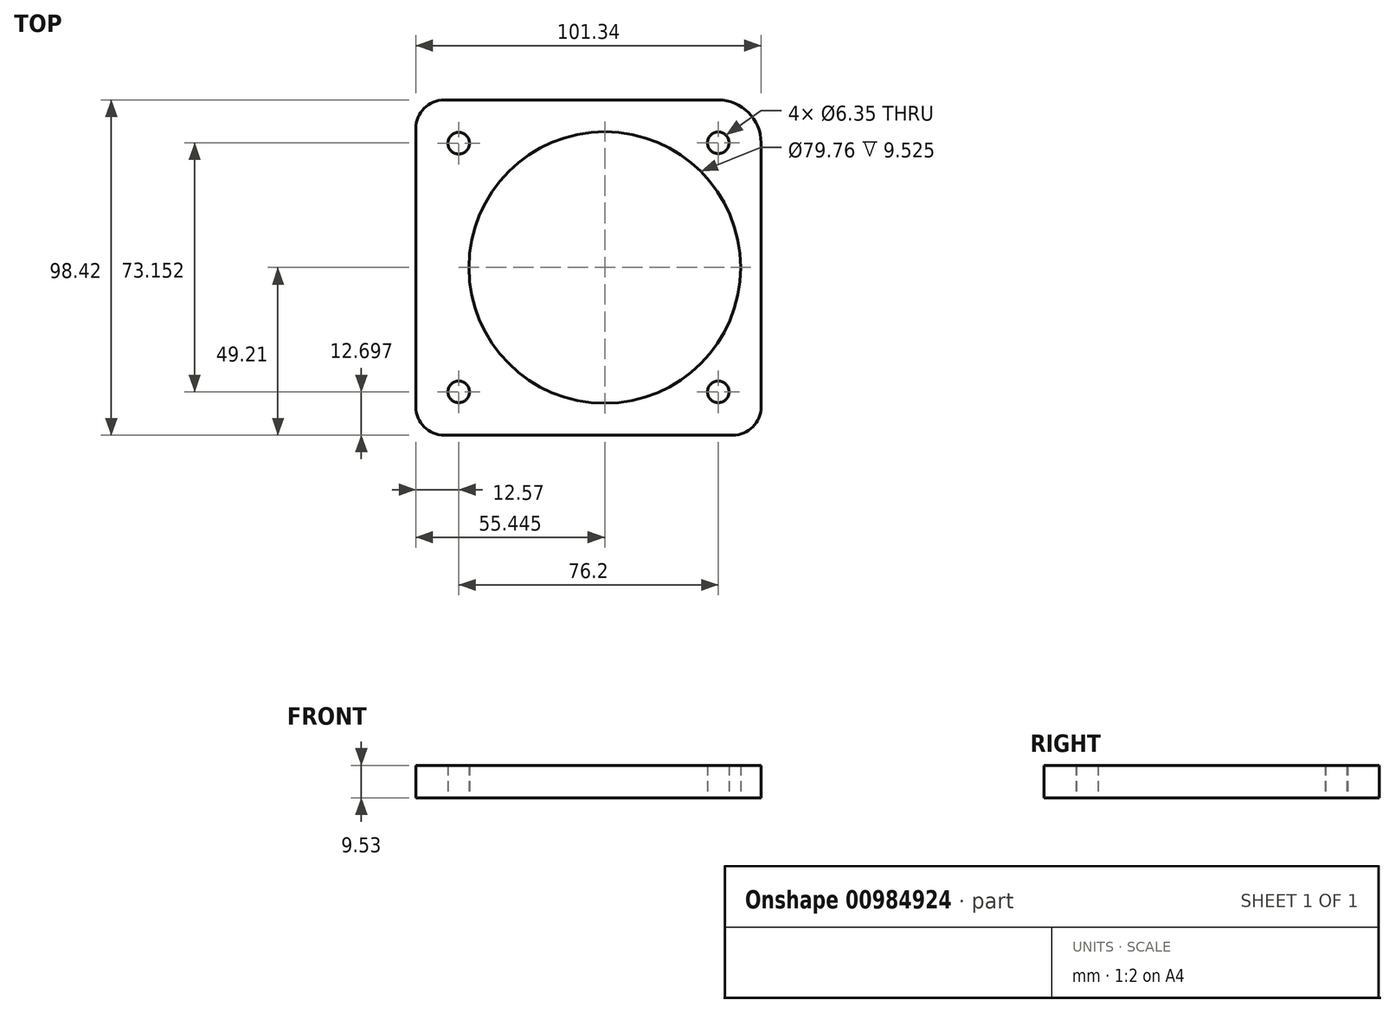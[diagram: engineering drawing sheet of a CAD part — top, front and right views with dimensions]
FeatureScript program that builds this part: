
annotation { "Feature Type Name" : "Feature", "Feature Type Description" : "" }
export const myFeature = defineFeature(function(context is Context, id is Id, definition is map)
    precondition{}
    {
        {
            var Q0;
            Q0=qCreatedBy(makeId("Top.planeOp"),FACE);
            var sketch = newSketch(context, id + "F0", { "sketchPlane" : qUnion([Q0])});
            skLineSegment(sketch, "E0.bottom", {"start": v(-42.39, 49.21) * mm, "end": v(38.1, 49.21) * mm});
            skLineSegment(sketch, "E0.top", {"start": v(-42.39, -49.21) * mm, "end": v(42.39, -49.21) * mm});
            skLineSegment(sketch, "E0.left", {"start": v(-50.67, 40.93) * mm, "end": v(-50.67, -40.93) * mm});
            skLineSegment(sketch, "E0.right", {"start": v(50.67, 36.64) * mm, "end": v(50.67, -40.93) * mm});
            skPoint(sketch, "E0.middle", {"position": v(0, 0) * mm});
            skCircle(sketch, "E1", {"center": v(4.78, 0) * mm, "radius": 39.88 * mm});
            skPoint(sketch, "E2.visualSharp", {"position": v(-50.67, 49.21) * mm});
            skArc(sketch, "E2.filletArc", {"start": v(-42.39, 49.21) * mm, "mid": v(-48.25, 46.79) * mm, "end": v(-50.67, 40.93) * mm});
            skPoint(sketch, "E3.visualSharp", {"position": v(-50.67, -49.21) * mm});
            skArc(sketch, "E3.filletArc", {"start": v(-50.67, -40.93) * mm, "mid": v(-48.25, -46.79) * mm, "end": v(-42.39, -49.21) * mm});
            skPoint(sketch, "E4.visualSharp", {"position": v(50.67, -49.21) * mm});
            skArc(sketch, "E4.filletArc", {"start": v(42.39, -49.21) * mm, "mid": v(48.25, -46.79) * mm, "end": v(50.67, -40.93) * mm});
            skPoint(sketch, "E5.visualSharp", {"position": v(50.67, 49.21) * mm});
            skArc(sketch, "E5.filletArc", {"start": v(50.67, 36.64) * mm, "mid": v(47, 45.53) * mm, "end": v(38.1, 49.21) * mm});
            skCircle(sketch, "E6", {"center": v(-38.1, 36.51) * mm, "radius": 3.18 * mm});
            skCircle(sketch, "E7", {"center": v(-38.1, -36.51) * mm, "radius": 3.18 * mm});
            skCircle(sketch, "E8", {"center": v(38.1, -36.51) * mm, "radius": 3.18 * mm});
            skCircle(sketch, "E9", {"center": v(38.1, 36.64) * mm, "radius": 3.18 * mm});
            skSolve(sketch);
        }
        {
            var Q0;
            Q0=makeQuery(id+"F0.imprint","IMPRINT",FACE,{"disambiguationData":[TD([[makeQuery(id+"F0.imprint","IMPRINT",EDGE,{"derivedFrom":sQuery(id+"F0.wireOp",EDGE,"E0.bottom")}),-1.0]])]});
            extrude(context, id + "F1", {"entities" : qUnion([Q0]), "depth" : 9.52 * mm, "offsetDistance" : 25.4 * mm});
        }
    });
